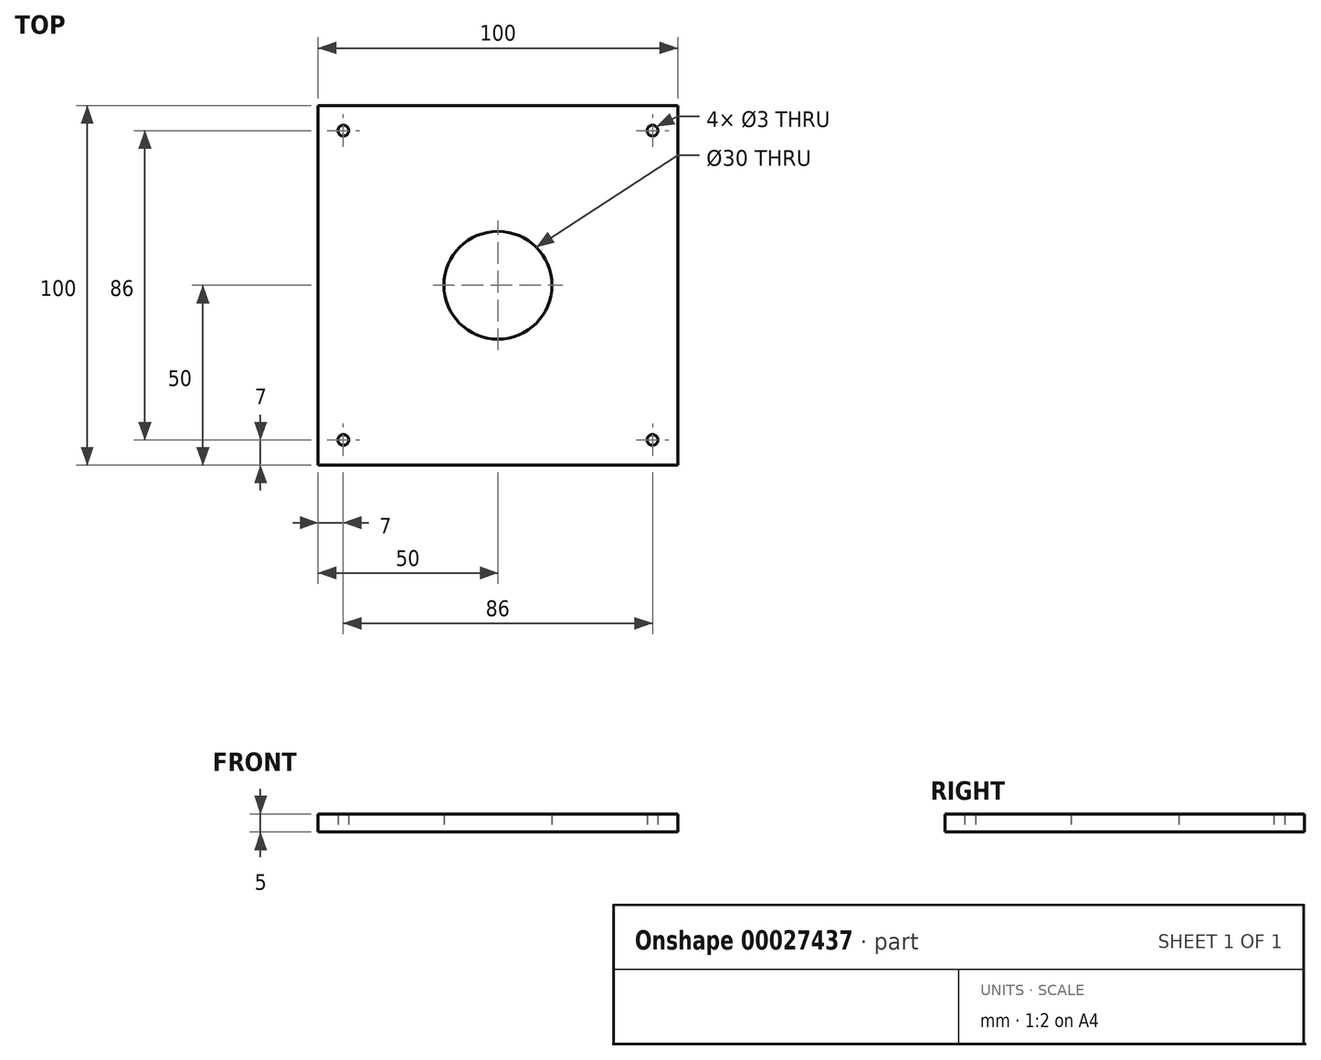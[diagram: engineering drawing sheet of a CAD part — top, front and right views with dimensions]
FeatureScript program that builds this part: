
annotation { "Feature Type Name" : "Feature", "Feature Type Description" : "" }
export const myFeature = defineFeature(function(context is Context, id is Id, definition is map)
    precondition{}
    {
        {
            var Q0;
            Q0=qCreatedBy(makeId("Top.planeOp"),FACE);
            var sketch = newSketch(context, id + "F0", { "sketchPlane" : qUnion([Q0])});
            skLineSegment(sketch, "E0.rect.bottom", {"start": v(50, 50) * mm, "end": v(-50, 50) * mm});
            skLineSegment(sketch, "E0.rect.top", {"start": v(50, -50) * mm, "end": v(-50, -50) * mm});
            skLineSegment(sketch, "E0.rect.left", {"start": v(50, 50) * mm, "end": v(50, -50) * mm});
            skLineSegment(sketch, "E0.rect.right", {"start": v(-50, 50) * mm, "end": v(-50, -50) * mm});
            skPoint(sketch, "E0.rect.middle", {"position": v(0, 0) * mm});
            skCircle(sketch, "E1", {"center": v(-43, 43) * mm, "radius": 1.5 * mm});
            skCircle(sketch, "E2", {"center": v(43, 43) * mm, "radius": 1.5 * mm});
            skLineSegment(sketch, "E3", {"start": v(-50, 0) * mm, "end": v(50, 0) * mm, "construction": true});
            skCircle(sketch, "E4.MirrorC", {"center": v(-43, -43) * mm, "radius": 1.5 * mm});
            skCircle(sketch, "E5.MirrorC", {"center": v(43, -43) * mm, "radius": 1.5 * mm});
            skLineSegment(sketch, "E6", {"start": v(0, 50) * mm, "end": v(0, -50) * mm, "construction": true});
            skCircle(sketch, "E7", {"center": v(0, 0) * mm, "radius": 15 * mm});
            skSolve(sketch);
        }
        {
            var Q0;
            Q0=makeQuery(id+"F0.imprint","IMPRINT",FACE,{"disambiguationData":[TD([[makeQuery(id+"F0.imprint","IMPRINT",EDGE,{"derivedFrom":sQuery(id+"F0.wireOp",EDGE,"E0.rect.bottom")}),1.0]])]});
            extrude(context, id + "F1", {"entities" : qUnion([Q0]), "depth" : 5 * mm});
        }
    });
